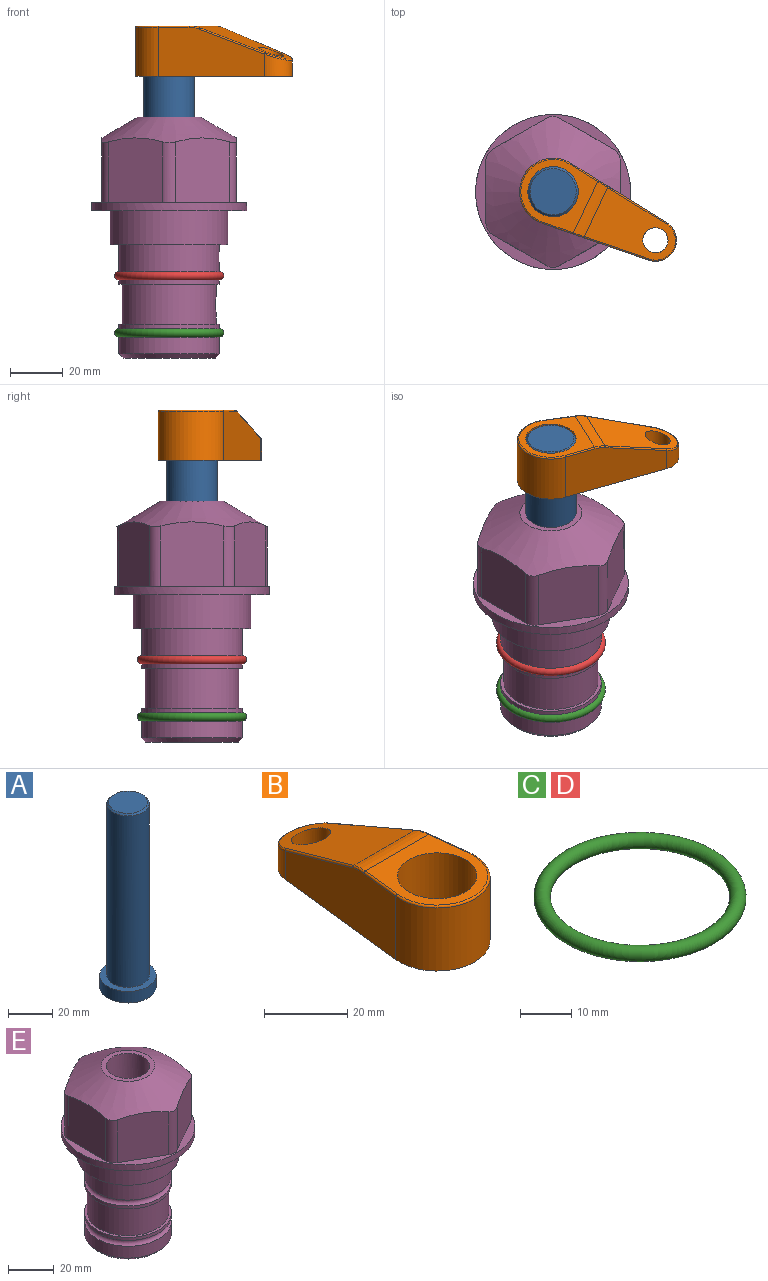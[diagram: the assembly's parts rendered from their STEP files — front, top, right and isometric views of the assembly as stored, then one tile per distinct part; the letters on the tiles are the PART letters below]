
ASSEMBLY  parts=5 mates=3
PART A: 6 faces, bbox 25.4x25.4x101.6 mm
  f0: plane 17.46x17.46mm, normal (0,0,1), area 239.5mm2, adj f5
  f1: plane 25.4x25.4mm, normal (0,0,-1), area 506.7mm2, adj f2
  f2: cylinder r=12.7mm len=25.4mm, axis (0,0,1), area 506.7mm2, adj f1,f3
  f3: plane 25.4x25.4mm, normal (0,0,1), area 221.7mm2, adj f2,f4
  f4: cylinder r=9.53mm len=94.46mm, axis (0,0,1), area 5653mm2, adj f3,f5
  f5: cone r=8.73mm half-angle=45deg, axis (0,0,-1), area 64.4mm2, adj f0,f4
PART B: 44 faces, bbox 27.5x64.5x19.1 mm
  f0: plane 2.3x0.95mm, normal (0,0,-1), area 1mm2, adj f25,f30,f34
  f1: plane 63.5x25.4mm, normal (0,0,-1), area 561.7mm2, adj f2,f3,f4,f5,f6,f7,f19,f20
  f2: cylinder r=12.7mm len=25.4mm, axis (0,0,-1), area 792.2mm2, adj f1,f3,f5,f13
  f3: plane 42.33x18.54mm, normal (0.99,0.11,0), area 647mm2, adj f1,f2,f4,f11,f12,f14
  f4: cylinder r=7.94mm len=15.78mm, axis (0,0,-1), area 158.6mm2, adj f1,f3,f5,f16
  f5: plane 42.33x18.54mm, normal (-0.99,0.11,0), area 647mm2, adj f1,f2,f4,f15,f17,f18
  f6: cylinder r=9.53mm len=19.05mm, axis (0,0,-1), area 1140.1mm2, adj f1,f8
  f7: cylinder r=4.76mm len=10.98mm, axis (0,0,-1), area 276.1mm2, adj f1,f9
  f8: plane 25.83x24.38mm, normal (0,0,1), area 262.2mm2, adj f6,f10,f11,f13,f15
  f9: plane 32.49x20.55mm, normal (0,0.34,0.94), area 489.9mm2, adj f7,f10,f14,f16,f18
  f10: cylinder r=12.7mm len=21.49mm, axis (-1,0,0), area 93.2mm2, adj f8,f9,f12,f17
  f11: cylinder r=0.51mm len=12.34mm, axis (0.11,-0.99,0), area 9.9mm2, adj f3,f8,f12,f13
  f12: bspline ~7.62x1.64mm, area 3.5mm2, adj f3,f10,f11,f14
  f13: torus R=12.19mm, axis (0,0,1), area 33.6mm2, adj f2,f8,f11,f15
  f14: cylinder r=0.51mm len=26.01mm, axis (0.1,-0.93,0.34), area 21.6mm2, adj f3,f9,f12,f16
  f15: cylinder r=0.51mm len=12.34mm, axis (0.11,0.99,0), area 9.9mm2, adj f5,f8,f13,f17
  f16: bspline ~15.78x7.05mm, area 15.7mm2, adj f4,f9,f14,f18
  f17: bspline ~7.62x1.64mm, area 3.5mm2, adj f5,f10,f15,f18
  f18: cylinder r=0.51mm len=26.01mm, axis (0.1,0.93,-0.34), area 21.6mm2, adj f5,f9,f16,f17
  f19: plane 21.6x14.29mm, normal (-0.99,-0.11,0), area 242.6mm2, adj f1,f26,f28,f34,f36,f38
  f20: plane 21.6x14.29mm, normal (0.99,-0.11,0), area 242.6mm2, adj f1,f27,f29,f37,f39,f41
  f21: cylinder r=12.7mm len=14.29mm, axis (0,0,-1), area 173.2mm2, adj f1,f26,f27,f30,f31,f33
  f22: cylinder r=7.94mm len=7.63mm, axis (0,0,-1), area 53.8mm2, adj f1,f28,f29,f42
  f23: plane 2.3x0.95mm, normal (0,0,-1), area 1mm2, adj f25,f33,f37
  f24: plane 17.94x12.32mm, normal (0,-0.34,-0.94), area 191.2mm2, adj f25,f38,f41,f42
  f25: cylinder r=9.53mm len=12.93mm, axis (-1,0,0), area 37.5mm2, adj f0,f23,f24,f31,f36,f39
  f26: cylinder r=1.59mm len=14.29mm, axis (0,0,-1), area 49mm2, adj f1,f19,f21,f32
  f27: cylinder r=1.59mm len=14.29mm, axis (0,0,-1), area 49mm2, adj f1,f20,f21,f35
  f28: cylinder r=1.59mm len=7.28mm, axis (0,0,-1), area 22.1mm2, adj f1,f19,f22,f40
  f29: cylinder r=1.59mm len=7.28mm, axis (0,0,-1), area 22.1mm2, adj f1,f20,f22,f43
  f30: torus R=14.29mm, axis (0,0,1), area 5.8mm2, adj f0,f21,f31,f32
  f31: bspline ~11.06x2.73mm, area 20.8mm2, adj f21,f25,f30,f33
  f32: sphere r=1.59mm, area 5.4mm2, adj f26,f30,f34
  f33: torus R=14.29mm, axis (0,0,1), area 5.8mm2, adj f21,f23,f31,f35
  f34: cylinder r=1.59mm len=1.68mm, axis (-0.11,0.99,0), area 2.4mm2, adj f0,f19,f32,f36
  f35: sphere r=1.59mm, area 5.4mm2, adj f27,f33,f37
  f36: bspline ~5.82x2.33mm, area 7.7mm2, adj f19,f25,f34,f38
  f37: cylinder r=1.59mm len=1.68mm, axis (0.11,0.99,0), area 2.4mm2, adj f20,f23,f35,f39
  f38: cylinder r=1.59mm len=18.33mm, axis (0.1,-0.93,0.34), area 46.7mm2, adj f19,f24,f36,f40
  f39: bspline ~5.82x2.33mm, area 7.7mm2, adj f20,f25,f37,f41
  f40: sphere r=1.59mm, area 3.6mm2, adj f28,f38,f42
  f41: cylinder r=1.59mm len=18.33mm, axis (0.1,0.93,-0.34), area 46.7mm2, adj f20,f24,f39,f43
  f42: bspline ~8.31x1.84mm, area 15.3mm2, adj f22,f24,f40,f43
  f43: sphere r=1.59mm, area 3.6mm2, adj f29,f41,f42
PART C: 1 faces, bbox 44.7x44.7x3.2 mm
  f0: torus R=19.05mm, axis (0,0,1), area 1193.9mm2
PART D: same geometry as C
PART E: 36 faces, bbox 58.7x58.7x91.2 mm
  f0: cylinder r=17.78mm len=35.56mm, axis (0,0,1), area 1670.8mm2, adj f23,f24,f31
  f1: cylinder r=19.05mm len=38.1mm, axis (0,0,1), area 1191.9mm2, adj f26,f27,f30
  f2: plane 58.66x58.66mm, normal (0,0,-1), area 1150.6mm2, adj f3,f28
  f3: cylinder r=29.33mm len=58.66mm, axis (0,0,-1), area 585.1mm2, adj f2,f4
  f4: plane 58.66x58.66mm, normal (0,0,1), area 475.9mm2, adj f3,f5,f6,f7,f8,f9,f10,f11
  f5: plane 24.5x20.32mm, normal (-0.5,0.87,0), area 562.8mm2, adj f4,f15,f16,f17
  f6: plane 24.5x20.32mm, normal (0.5,0.87,0), area 562.8mm2, adj f4,f14,f15,f17
  f7: plane 24.5x23.48mm, normal (1,0,0), area 562.8mm2, adj f4,f13,f14,f17
  f8: plane 24.5x20.32mm, normal (0.5,-0.87,0), area 562.8mm2, adj f4,f12,f13,f17
  f9: plane 24.5x20.32mm, normal (-0.5,-0.87,0), area 562.8mm2, adj f4,f11,f12,f17
  f10: plane 24.5x23.48mm, normal (-1,0,0), area 562.8mm2, adj f4,f11,f16,f17
  f11: cylinder r=5.08mm len=23.01mm, axis (0,0,-1), area 121.2mm2, adj f4,f9,f10,f17
  f12: cylinder r=5.08mm len=23.01mm, axis (0,0,-1), area 121.2mm2, adj f4,f8,f9,f17
  f13: cylinder r=5.08mm len=23.01mm, axis (0,0,-1), area 121.2mm2, adj f4,f7,f8,f17
  f14: cylinder r=5.08mm len=23.01mm, axis (0,0,-1), area 121.2mm2, adj f4,f6,f7,f17
  f15: cylinder r=5.08mm len=23.01mm, axis (0,0,-1), area 121.2mm2, adj f4,f5,f6,f17
  f16: cylinder r=5.08mm len=23.01mm, axis (0,0,-1), area 121.2mm2, adj f4,f5,f10,f17
  f17: cone r=11.73mm half-angle=60deg, axis (0,0,-1), area 2071.8mm2, adj f5,f6,f7,f8,f9,f10,f11,f12
  f18: plane 23.46x23.46mm, normal (0,0,1), area 147.4mm2, adj f17,f35
  f19: plane 34.93x34.93mm, normal (0,0,-1), area 958mm2, adj f29
  f20: cylinder r=19.05mm len=38.1mm, axis (0,0,1), area 760.1mm2, adj f21,f29
  f21: torus R=19.05mm, axis (0,0,1), area 565.3mm2, adj f20,f22
  f22: cylinder r=19.05mm len=38.1mm, axis (0,0,1), area 190mm2, adj f21,f23
  f23: plane 38.1x38.1mm, normal (0,0,1), area 146.9mm2, adj f0,f22
  f24: plane 38.1x38.1mm, normal (0,0,-1), area 146.9mm2, adj f0,f25
  f25: cylinder r=19.05mm len=38.1mm, axis (0,0,1), area 190mm2, adj f24,f26
  f26: torus R=19.05mm, axis (0,0,1), area 565.3mm2, adj f1,f25
  f27: plane 44.45x44.45mm, normal (0,0,-1), area 411.7mm2, adj f1,f28
  f28: cylinder r=22.23mm len=44.45mm, axis (0,0,1), area 1773.5mm2, adj f2,f27
  f29: cone r=19.05mm half-angle=45deg, axis (0,0,1), area 257.5mm2, adj f19,f20
  f30: cylinder r=3.17mm len=6.75mm, axis (-1,0,0), area 128mm2, adj f1,f33
  f31: cylinder r=3.17mm len=6.35mm, axis (-1,0,0), area 102.5mm2, adj f0,f33
  f32: plane 25.4x25.4mm, normal (0,0,1), area 506.7mm2, adj f33
  f33: cylinder r=12.7mm len=66.42mm, axis (0,0,-1), area 5236.2mm2, adj f30,f31,f32,f34
  f34: cone r=9.53mm half-angle=30deg, axis (0,0,-1), area 443.4mm2, adj f33,f35
  f35: cylinder r=9.53mm len=19.05mm, axis (0,0,-1), area 849mm2, adj f18,f34
PLACE A rot(axis=(0,0,-1),25.4deg) t=(0,0,-3.66)mm
PLACE B rot(axis=(0,0,-1),115.4deg) t=(0,0,50.95)mm
PLACE C t=(0,0,-21.59)mm
PLACE D at identity
PLACE E at identity fixed
MATE fastened C.f0 <-> E.f0  axis (0,0,1) through (0,0,-46.1)mm
MATE cylindrical A.f2 <-> E.f0  axis (0,0,1) through (0,0,21.98)mm
MATE fastened B.f2 <-> A.f2  axis (0,0,1) through (0,0,70)mm
